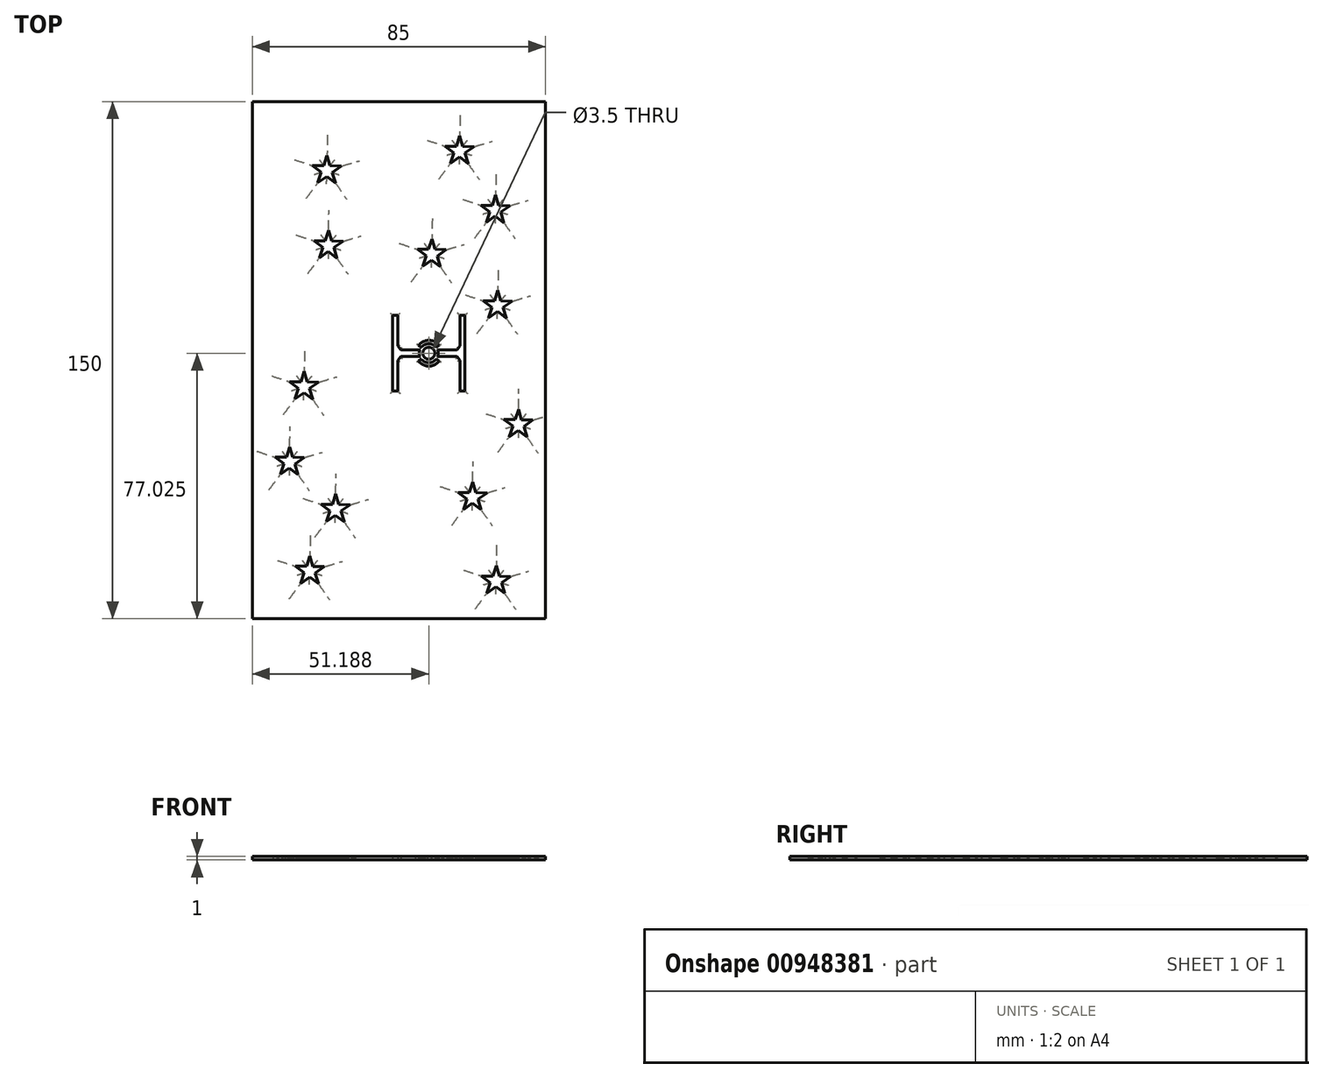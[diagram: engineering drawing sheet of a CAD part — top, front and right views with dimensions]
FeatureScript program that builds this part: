
annotation { "Feature Type Name" : "Feature", "Feature Type Description" : "" }
export const myFeature = defineFeature(function(context is Context, id is Id, definition is map)
    precondition{}
    {
        {
            var Q0;
            Q0=qCreatedBy(makeId("Top.planeOp"),FACE);
            var sketch = newSketch(context, id + "F0", { "sketchPlane" : qUnion([Q0])});
            skLineSegment(sketch, "E0.top", {"start": v(42.5, -75) * mm, "end": v(-42.5, -75) * mm});
            skLineSegment(sketch, "E0.left", {"start": v(42.5, 75) * mm, "end": v(42.5, -75) * mm});
            skLineSegment(sketch, "E0.right", {"start": v(-42.5, 75) * mm, "end": v(-42.5, -75) * mm});
            skLineSegment(sketch, "E1", {"start": v(-42.5, 75) * mm, "end": v(42.5, 75) * mm});
            skLineSegment(sketch, "E2", {"start": v(-1.81, 13.03) * mm, "end": v(-0.31, 13.03) * mm});
            skLineSegment(sketch, "E3", {"start": v(-0.31, 13.03) * mm, "end": v(-0.31, 4.14) * mm});
            skLineSegment(sketch, "E4", {"start": v(-0.31, 4.14) * mm, "end": v(0.54, 3) * mm});
            skLineSegment(sketch, "E5", {"start": v(0.54, 3) * mm, "end": v(6.12, 3) * mm});
            skLineSegment(sketch, "E6", {"start": v(-1.81, 13.03) * mm, "end": v(-1.81, -8.97) * mm});
            skPoint(sketch, "E7.endSnap0", {"position": v(-0.31, 8.58) * mm});
            skLineSegment(sketch, "E8.MirrorCS", {"start": v(0.54, 1.05) * mm, "end": v(6.12, 1.05) * mm});
            skLineSegment(sketch, "E9.MirrorCS", {"start": v(-0.31, -0.09) * mm, "end": v(0.54, 1.05) * mm});
            skLineSegment(sketch, "E10.MirrorCS", {"start": v(-0.31, -8.97) * mm, "end": v(-0.31, -0.09) * mm});
            skLineSegment(sketch, "E11.MirrorCS", {"start": v(-1.81, -8.97) * mm, "end": v(-0.31, -8.97) * mm});
            skLineSegment(sketch, "E12.MirrorCS", {"start": v(16.84, 3) * mm, "end": v(11.26, 3) * mm});
            skLineSegment(sketch, "E13.MirrorCS", {"start": v(16.84, 1.05) * mm, "end": v(11.26, 1.05) * mm});
            skLineSegment(sketch, "E14.MirrorCS", {"start": v(17.69, -0.09) * mm, "end": v(16.84, 1.05) * mm});
            skLineSegment(sketch, "E15.MirrorCS", {"start": v(17.69, 4.14) * mm, "end": v(16.84, 3) * mm});
            skLineSegment(sketch, "E16.MirrorCS", {"start": v(17.69, -8.97) * mm, "end": v(17.69, -0.09) * mm});
            skLineSegment(sketch, "E17.MirrorCS", {"start": v(19.19, -8.97) * mm, "end": v(17.69, -8.97) * mm});
            skLineSegment(sketch, "E18.MirrorCS", {"start": v(19.19, 13.03) * mm, "end": v(19.19, -8.97) * mm});
            skLineSegment(sketch, "E19.MirrorCS", {"start": v(19.19, 13.03) * mm, "end": v(17.69, 13.03) * mm});
            skLineSegment(sketch, "E20.MirrorCS", {"start": v(17.69, 13.03) * mm, "end": v(17.69, 4.14) * mm});
            skCircle(sketch, "E21", {"center": v(8.69, 2.03) * mm, "radius": 2.75 * mm});
            skCircle(sketch, "E22", {"center": v(8.69, 2.03) * mm, "radius": 1.75 * mm});
            skCircle(sketch, "E23", {"center": v(8.69, 2.03) * mm, "radius": 3.75 * mm});
            skLineSegment(sketch, "E24", {"start": v(6.52, 0.34) * mm, "end": v(5.69, -0.22) * mm});
            skLineSegment(sketch, "E25.MirrorCS", {"start": v(10.86, 0.34) * mm, "end": v(11.69, -0.22) * mm});
            skLineSegment(sketch, "E26.MirrorCS", {"start": v(6.52, 3.72) * mm, "end": v(5.69, 4.27) * mm});
            skLineSegment(sketch, "E27.MirrorCS", {"start": v(10.86, 3.72) * mm, "end": v(11.69, 4.27) * mm});
            skLineSegment(sketch, "E28", {"start": v(-20.37, 37.63) * mm, "end": v(-21.34, 34.62) * mm});
            skPoint(sketch, "E28.startSnap0", {"position": v(-20.37, 37.8) * mm});
            skLineSegment(sketch, "E29", {"start": v(-21.34, 34.62) * mm, "end": v(-24.61, 34.62) * mm});
            skLineSegment(sketch, "E30", {"start": v(-24.61, 34.62) * mm, "end": v(-22.04, 32.72) * mm});
            skLineSegment(sketch, "E31", {"start": v(-22.04, 32.72) * mm, "end": v(-23.07, 29.65) * mm});
            skLineSegment(sketch, "E32", {"start": v(-23.07, 29.65) * mm, "end": v(-20.47, 31.51) * mm});
            skLineSegment(sketch, "E33", {"start": v(-20.37, 37.63) * mm, "end": v(-20.47, 31.51) * mm, "construction": true});
            skLineSegment(sketch, "E34.MirrorCS", {"start": v(-17.93, 29.57) * mm, "end": v(-20.47, 31.51) * mm});
            skLineSegment(sketch, "E35.MirrorCS", {"start": v(-18.86, 32.67) * mm, "end": v(-17.93, 29.57) * mm});
            skLineSegment(sketch, "E36.MirrorCS", {"start": v(-16.23, 34.5) * mm, "end": v(-18.86, 32.67) * mm});
            skLineSegment(sketch, "E37.MirrorCS", {"start": v(-20.37, 37.63) * mm, "end": v(-19.5, 34.6) * mm});
            skLineSegment(sketch, "E38.MirrorCS", {"start": v(-19.5, 34.6) * mm, "end": v(-16.23, 34.5) * mm});
            skLineSegment(sketch, "E39", {"start": v(9.58, 35.19) * mm, "end": v(8.62, 32.18) * mm});
            skLineSegment(sketch, "E40", {"start": v(8.62, 32.18) * mm, "end": v(5.35, 32.18) * mm});
            skLineSegment(sketch, "E41", {"start": v(5.35, 32.18) * mm, "end": v(7.92, 30.28) * mm});
            skLineSegment(sketch, "E42", {"start": v(7.92, 30.28) * mm, "end": v(6.89, 27.2) * mm});
            skLineSegment(sketch, "E43", {"start": v(6.89, 27.2) * mm, "end": v(9.49, 29.07) * mm});
            skLineSegment(sketch, "E44.MirrorCS", {"start": v(12.03, 27.13) * mm, "end": v(9.49, 29.07) * mm});
            skLineSegment(sketch, "E45.MirrorCS", {"start": v(11.1, 30.23) * mm, "end": v(12.03, 27.13) * mm});
            skLineSegment(sketch, "E46.MirrorCS", {"start": v(13.73, 32.05) * mm, "end": v(11.1, 30.23) * mm});
            skLineSegment(sketch, "E47.MirrorCS", {"start": v(9.58, 35.19) * mm, "end": v(10.46, 32.15) * mm});
            skLineSegment(sketch, "E48.MirrorCS", {"start": v(10.46, 32.15) * mm, "end": v(13.73, 32.05) * mm});
            skLineSegment(sketch, "E49", {"start": v(-20.83, 59.45) * mm, "end": v(-21.8, 56.44) * mm});
            skLineSegment(sketch, "E50", {"start": v(-21.8, 56.44) * mm, "end": v(-25.06, 56.44) * mm});
            skLineSegment(sketch, "E51", {"start": v(-25.06, 56.44) * mm, "end": v(-22.5, 54.54) * mm});
            skLineSegment(sketch, "E52", {"start": v(-22.5, 54.54) * mm, "end": v(-23.52, 51.47) * mm});
            skLineSegment(sketch, "E53", {"start": v(-23.52, 51.47) * mm, "end": v(-20.92, 53.34) * mm});
            skLineSegment(sketch, "E54.MirrorCS", {"start": v(-18.38, 51.39) * mm, "end": v(-20.92, 53.34) * mm});
            skLineSegment(sketch, "E55.MirrorCS", {"start": v(-19.31, 54.5) * mm, "end": v(-18.38, 51.39) * mm});
            skLineSegment(sketch, "E56.MirrorCS", {"start": v(-16.68, 56.32) * mm, "end": v(-19.31, 54.5) * mm});
            skLineSegment(sketch, "E57.MirrorCS", {"start": v(-20.83, 59.45) * mm, "end": v(-19.95, 56.42) * mm});
            skLineSegment(sketch, "E58.MirrorCS", {"start": v(-19.95, 56.42) * mm, "end": v(-16.68, 56.32) * mm});
            skLineSegment(sketch, "E59", {"start": v(28.7, 20.23) * mm, "end": v(27.73, 17.23) * mm});
            skLineSegment(sketch, "E60", {"start": v(27.73, 17.23) * mm, "end": v(24.46, 17.23) * mm});
            skLineSegment(sketch, "E61", {"start": v(24.46, 17.23) * mm, "end": v(27.03, 15.32) * mm});
            skLineSegment(sketch, "E62", {"start": v(27.03, 15.32) * mm, "end": v(26, 12.25) * mm});
            skLineSegment(sketch, "E63", {"start": v(26, 12.25) * mm, "end": v(28.6, 14.12) * mm});
            skLineSegment(sketch, "E64.MirrorCS", {"start": v(31.14, 12.17) * mm, "end": v(28.6, 14.12) * mm});
            skLineSegment(sketch, "E65.MirrorCS", {"start": v(30.2, 15.27) * mm, "end": v(31.14, 12.17) * mm});
            skLineSegment(sketch, "E66.MirrorCS", {"start": v(32.84, 17.1) * mm, "end": v(30.2, 15.27) * mm});
            skLineSegment(sketch, "E67.MirrorCS", {"start": v(28.7, 20.23) * mm, "end": v(29.57, 17.2) * mm});
            skLineSegment(sketch, "E68.MirrorCS", {"start": v(29.57, 17.2) * mm, "end": v(32.84, 17.1) * mm});
            skLineSegment(sketch, "E69", {"start": v(21.4, -35.35) * mm, "end": v(20.44, -38.35) * mm});
            skLineSegment(sketch, "E70", {"start": v(20.44, -38.35) * mm, "end": v(17.17, -38.35) * mm});
            skLineSegment(sketch, "E71", {"start": v(17.17, -38.35) * mm, "end": v(19.74, -40.26) * mm});
            skLineSegment(sketch, "E72", {"start": v(19.74, -40.26) * mm, "end": v(18.71, -43.33) * mm});
            skLineSegment(sketch, "E73", {"start": v(18.71, -43.33) * mm, "end": v(21.31, -41.46) * mm});
            skLineSegment(sketch, "E74.MirrorCS", {"start": v(23.86, -43.41) * mm, "end": v(21.31, -41.46) * mm});
            skLineSegment(sketch, "E75.MirrorCS", {"start": v(22.92, -40.3) * mm, "end": v(23.86, -43.41) * mm});
            skLineSegment(sketch, "E76.MirrorCS", {"start": v(25.55, -38.48) * mm, "end": v(22.92, -40.3) * mm});
            skLineSegment(sketch, "E77.MirrorCS", {"start": v(21.4, -35.35) * mm, "end": v(22.28, -38.38) * mm});
            skLineSegment(sketch, "E78.MirrorCS", {"start": v(22.28, -38.38) * mm, "end": v(25.55, -38.48) * mm});
            skLineSegment(sketch, "E79", {"start": v(-18.3, -38.84) * mm, "end": v(-19.28, -41.84) * mm});
            skLineSegment(sketch, "E80", {"start": v(-19.28, -41.84) * mm, "end": v(-22.55, -41.84) * mm});
            skLineSegment(sketch, "E81", {"start": v(-22.55, -41.84) * mm, "end": v(-19.97, -43.75) * mm});
            skLineSegment(sketch, "E82", {"start": v(-19.97, -43.75) * mm, "end": v(-21, -46.82) * mm});
            skLineSegment(sketch, "E83", {"start": v(-21, -46.82) * mm, "end": v(-18.4, -44.95) * mm});
            skLineSegment(sketch, "E84.MirrorCS", {"start": v(-15.86, -46.9) * mm, "end": v(-18.4, -44.95) * mm});
            skLineSegment(sketch, "E85.MirrorCS", {"start": v(-16.8, -43.8) * mm, "end": v(-15.86, -46.9) * mm});
            skLineSegment(sketch, "E86.MirrorCS", {"start": v(-14.17, -41.97) * mm, "end": v(-16.8, -43.8) * mm});
            skLineSegment(sketch, "E87.MirrorCS", {"start": v(-18.3, -38.84) * mm, "end": v(-17.43, -41.87) * mm});
            skLineSegment(sketch, "E88.MirrorCS", {"start": v(-17.43, -41.87) * mm, "end": v(-14.17, -41.97) * mm});
            skLineSegment(sketch, "E89", {"start": v(-27.45, -3.28) * mm, "end": v(-28.42, -6.28) * mm});
            skLineSegment(sketch, "E90", {"start": v(-28.42, -6.28) * mm, "end": v(-31.69, -6.28) * mm});
            skLineSegment(sketch, "E91", {"start": v(-31.69, -6.28) * mm, "end": v(-29.11, -8.19) * mm});
            skLineSegment(sketch, "E92", {"start": v(-29.11, -8.19) * mm, "end": v(-30.14, -11.26) * mm});
            skLineSegment(sketch, "E93", {"start": v(-30.14, -11.26) * mm, "end": v(-27.54, -9.4) * mm});
            skLineSegment(sketch, "E94.MirrorCS", {"start": v(-25, -11.34) * mm, "end": v(-27.54, -9.4) * mm});
            skLineSegment(sketch, "E95.MirrorCS", {"start": v(-25.93, -8.24) * mm, "end": v(-25, -11.34) * mm});
            skLineSegment(sketch, "E96.MirrorCS", {"start": v(-23.3, -6.41) * mm, "end": v(-25.93, -8.24) * mm});
            skLineSegment(sketch, "E97.MirrorCS", {"start": v(-27.45, -3.28) * mm, "end": v(-26.57, -6.31) * mm});
            skLineSegment(sketch, "E98.MirrorCS", {"start": v(-26.57, -6.31) * mm, "end": v(-23.3, -6.41) * mm});
            skLineSegment(sketch, "E99", {"start": v(28.22, -59.61) * mm, "end": v(27.25, -62.62) * mm});
            skLineSegment(sketch, "E100", {"start": v(27.25, -62.62) * mm, "end": v(23.98, -62.62) * mm});
            skLineSegment(sketch, "E101", {"start": v(23.98, -62.62) * mm, "end": v(26.55, -64.52) * mm});
            skLineSegment(sketch, "E102", {"start": v(26.55, -64.52) * mm, "end": v(25.52, -67.6) * mm});
            skLineSegment(sketch, "E103", {"start": v(25.52, -67.6) * mm, "end": v(28.13, -65.72) * mm});
            skLineSegment(sketch, "E104.MirrorCS", {"start": v(30.67, -67.67) * mm, "end": v(28.13, -65.72) * mm});
            skLineSegment(sketch, "E105.MirrorCS", {"start": v(29.73, -64.57) * mm, "end": v(30.67, -67.67) * mm});
            skLineSegment(sketch, "E106.MirrorCS", {"start": v(32.36, -62.75) * mm, "end": v(29.73, -64.57) * mm});
            skLineSegment(sketch, "E107.MirrorCS", {"start": v(28.22, -59.61) * mm, "end": v(29.1, -62.64) * mm});
            skLineSegment(sketch, "E108.MirrorCS", {"start": v(29.1, -62.64) * mm, "end": v(32.36, -62.75) * mm});
            skLineSegment(sketch, "E109", {"start": v(34.7, -14.25) * mm, "end": v(33.73, -17.25) * mm});
            skLineSegment(sketch, "E110", {"start": v(33.73, -17.25) * mm, "end": v(30.46, -17.25) * mm});
            skLineSegment(sketch, "E111", {"start": v(30.46, -17.25) * mm, "end": v(33.04, -19.15) * mm});
            skLineSegment(sketch, "E112", {"start": v(33.04, -19.15) * mm, "end": v(32, -22.23) * mm});
            skLineSegment(sketch, "E113", {"start": v(32, -22.23) * mm, "end": v(34.6, -20.36) * mm});
            skLineSegment(sketch, "E114.MirrorCS", {"start": v(37.15, -22.3) * mm, "end": v(34.6, -20.36) * mm});
            skLineSegment(sketch, "E115.MirrorCS", {"start": v(36.22, -19.2) * mm, "end": v(37.15, -22.3) * mm});
            skLineSegment(sketch, "E116.MirrorCS", {"start": v(38.84, -17.38) * mm, "end": v(36.22, -19.2) * mm});
            skLineSegment(sketch, "E117.MirrorCS", {"start": v(34.7, -14.25) * mm, "end": v(35.58, -17.28) * mm});
            skLineSegment(sketch, "E118.MirrorCS", {"start": v(35.58, -17.28) * mm, "end": v(38.84, -17.38) * mm});
            skLineSegment(sketch, "E119", {"start": v(-25.79, -56.79) * mm, "end": v(-26.75, -59.8) * mm});
            skLineSegment(sketch, "E120", {"start": v(-26.75, -59.8) * mm, "end": v(-30.02, -59.8) * mm});
            skLineSegment(sketch, "E121", {"start": v(-30.02, -59.8) * mm, "end": v(-27.45, -61.7) * mm});
            skLineSegment(sketch, "E122", {"start": v(-27.45, -61.7) * mm, "end": v(-28.48, -64.77) * mm});
            skLineSegment(sketch, "E123", {"start": v(-28.48, -64.77) * mm, "end": v(-25.88, -62.9) * mm});
            skLineSegment(sketch, "E124.MirrorCS", {"start": v(-23.34, -64.85) * mm, "end": v(-25.88, -62.9) * mm});
            skLineSegment(sketch, "E125.MirrorCS", {"start": v(-24.27, -61.74) * mm, "end": v(-23.34, -64.85) * mm});
            skLineSegment(sketch, "E126.MirrorCS", {"start": v(-21.64, -59.92) * mm, "end": v(-24.27, -61.74) * mm});
            skLineSegment(sketch, "E127.MirrorCS", {"start": v(-25.79, -56.79) * mm, "end": v(-24.91, -59.82) * mm});
            skLineSegment(sketch, "E128.MirrorCS", {"start": v(-24.91, -59.82) * mm, "end": v(-21.64, -59.92) * mm});
            skLineSegment(sketch, "E129", {"start": v(17.65, 65.09) * mm, "end": v(16.68, 62.09) * mm});
            skLineSegment(sketch, "E130", {"start": v(16.68, 62.09) * mm, "end": v(13.41, 62.09) * mm});
            skLineSegment(sketch, "E131", {"start": v(13.41, 62.09) * mm, "end": v(15.98, 60.18) * mm});
            skLineSegment(sketch, "E132", {"start": v(15.98, 60.18) * mm, "end": v(14.95, 57.1) * mm});
            skLineSegment(sketch, "E133", {"start": v(14.95, 57.1) * mm, "end": v(17.55, 58.98) * mm});
            skLineSegment(sketch, "E134.MirrorCS", {"start": v(20.1, 57.03) * mm, "end": v(17.55, 58.98) * mm});
            skLineSegment(sketch, "E135.MirrorCS", {"start": v(19.16, 60.13) * mm, "end": v(20.1, 57.03) * mm});
            skLineSegment(sketch, "E136.MirrorCS", {"start": v(21.8, 61.96) * mm, "end": v(19.16, 60.13) * mm});
            skLineSegment(sketch, "E137.MirrorCS", {"start": v(17.65, 65.09) * mm, "end": v(18.52, 62.06) * mm});
            skLineSegment(sketch, "E138.MirrorCS", {"start": v(18.52, 62.06) * mm, "end": v(21.8, 61.96) * mm});
            skLineSegment(sketch, "E139", {"start": v(28.04, 47.95) * mm, "end": v(27.07, 44.94) * mm});
            skLineSegment(sketch, "E140", {"start": v(27.07, 44.94) * mm, "end": v(23.8, 44.94) * mm});
            skLineSegment(sketch, "E141", {"start": v(23.8, 44.94) * mm, "end": v(26.37, 43.04) * mm});
            skLineSegment(sketch, "E142", {"start": v(26.37, 43.04) * mm, "end": v(25.34, 39.97) * mm});
            skLineSegment(sketch, "E143", {"start": v(25.34, 39.97) * mm, "end": v(27.95, 41.84) * mm});
            skLineSegment(sketch, "E144.MirrorCS", {"start": v(30.49, 39.89) * mm, "end": v(27.95, 41.84) * mm});
            skLineSegment(sketch, "E145.MirrorCS", {"start": v(29.55, 43) * mm, "end": v(30.49, 39.89) * mm});
            skLineSegment(sketch, "E146.MirrorCS", {"start": v(32.18, 44.82) * mm, "end": v(29.55, 43) * mm});
            skLineSegment(sketch, "E147.MirrorCS", {"start": v(28.04, 47.95) * mm, "end": v(28.91, 44.92) * mm});
            skLineSegment(sketch, "E148.MirrorCS", {"start": v(28.91, 44.92) * mm, "end": v(32.18, 44.82) * mm});
            skLineSegment(sketch, "E149", {"start": v(-31.65, -25.14) * mm, "end": v(-32.62, -28.14) * mm});
            skLineSegment(sketch, "E150", {"start": v(-32.62, -28.14) * mm, "end": v(-35.89, -28.14) * mm});
            skLineSegment(sketch, "E151", {"start": v(-35.89, -28.14) * mm, "end": v(-33.32, -30.05) * mm});
            skLineSegment(sketch, "E152", {"start": v(-33.32, -30.05) * mm, "end": v(-34.35, -33.12) * mm});
            skLineSegment(sketch, "E153", {"start": v(-34.35, -33.12) * mm, "end": v(-31.75, -31.25) * mm});
            skLineSegment(sketch, "E154.MirrorCS", {"start": v(-29.2, -33.2) * mm, "end": v(-31.75, -31.25) * mm});
            skLineSegment(sketch, "E155.MirrorCS", {"start": v(-30.14, -30.1) * mm, "end": v(-29.2, -33.2) * mm});
            skLineSegment(sketch, "E156.MirrorCS", {"start": v(-27.5, -28.27) * mm, "end": v(-30.14, -30.1) * mm});
            skLineSegment(sketch, "E157.MirrorCS", {"start": v(-31.65, -25.14) * mm, "end": v(-30.78, -28.17) * mm});
            skLineSegment(sketch, "E158.MirrorCS", {"start": v(-30.78, -28.17) * mm, "end": v(-27.5, -28.27) * mm});
            skSolve(sketch);
        }
        {
            var Q0;
            Q0=makeQuery(id+"F0.imprint","IMPRINT",FACE,{"disambiguationData":[TD([[makeQuery(id+"F0.imprint","IMPRINT",EDGE,{"derivedFrom":sQuery(id+"F0.wireOp",EDGE,"E0.top")}),-1.0]])]});
            var Q1;
            Q1=makeQuery(id+"F0.imprint","IMPRINT",FACE,{"disambiguationData":[TD([[makeQuery(id+"F0.imprint","IMPRINT",EDGE,{"derivedFrom":sQuery(id+"F0.wireOp",EDGE,"E22")}),-1.0]])]});
            var Q2;
            {var subQ5=sQuery(id+"F0.wireOp",EDGE,"E24");Q2=makeQuery(id+"F0.imprint","IMPRINT",FACE,{"disambiguationData":[TD([[makeQuery(id+"F0.imprint","IMPRINT",EDGE,{"derivedFrom":subQ5}),-1.0]])]});}
            var Q3;
            {var subQ5=sQuery(id+"F0.wireOp",EDGE,"E26.MirrorCS");Q3=makeQuery(id+"F0.imprint","IMPRINT",FACE,{"disambiguationData":[TD([[makeQuery(id+"F0.imprint","IMPRINT",EDGE,{"derivedFrom":subQ5}),1.0]])]});}
            var Q4;
            {var subQ5=sQuery(id+"F0.wireOp",EDGE,"E25.MirrorCS");Q4=makeQuery(id+"F0.imprint","IMPRINT",FACE,{"disambiguationData":[TD([[makeQuery(id+"F0.imprint","IMPRINT",EDGE,{"derivedFrom":subQ5}),1.0]])]});}
            var Q5;
            {var subQ5=sQuery(id+"F0.wireOp",EDGE,"E27.MirrorCS");Q5=makeQuery(id+"F0.imprint","IMPRINT",FACE,{"disambiguationData":[TD([[makeQuery(id+"F0.imprint","IMPRINT",EDGE,{"derivedFrom":subQ5}),-1.0]])]});}
            extrude(context, id + "F1", {"entities" : qUnion([Q0, Q1, Q2, Q3, Q4, Q5]), "depth" : 1 * mm, "offsetDistance" : 25 * mm});
        }
        {
            var Q0;
            Q0=makeQuery(id+"F1.opExtrude","CAP_EDGE",EDGE,{"disambiguationData":[OSD([sQuery(id+"F0.wireOp",EDGE,"E147.MirrorCS")])],"isStart":true});
            var Q1;
            Q1=makeQuery(id+"F1.opExtrude","CAP_EDGE",EDGE,{"disambiguationData":[OSD([sQuery(id+"F0.wireOp",EDGE,"E148.MirrorCS")])],"isStart":true});
            var Q2;
            Q2=makeQuery(id+"F1.opExtrude","CAP_EDGE",EDGE,{"disambiguationData":[OSD([sQuery(id+"F0.wireOp",EDGE,"E146.MirrorCS")])],"isStart":true});
            var Q3;
            Q3=makeQuery(id+"F1.opExtrude","CAP_EDGE",EDGE,{"disambiguationData":[OSD([sQuery(id+"F0.wireOp",EDGE,"E145.MirrorCS")])],"isStart":true});
            var Q4;
            Q4=makeQuery(id+"F1.opExtrude","CAP_EDGE",EDGE,{"disambiguationData":[OSD([sQuery(id+"F0.wireOp",EDGE,"E144.MirrorCS")])],"isStart":true});
            var Q5;
            Q5=makeQuery(id+"F1.opExtrude","CAP_EDGE",EDGE,{"disambiguationData":[OSD([sQuery(id+"F0.wireOp",EDGE,"E143")])],"isStart":true});
            var Q6;
            Q6=makeQuery(id+"F1.opExtrude","CAP_EDGE",EDGE,{"disambiguationData":[OSD([sQuery(id+"F0.wireOp",EDGE,"E142")])],"isStart":true});
            var Q7;
            Q7=makeQuery(id+"F1.opExtrude","CAP_EDGE",EDGE,{"disambiguationData":[OSD([sQuery(id+"F0.wireOp",EDGE,"E141")])],"isStart":true});
            var Q8;
            Q8=makeQuery(id+"F1.opExtrude","CAP_EDGE",EDGE,{"disambiguationData":[OSD([sQuery(id+"F0.wireOp",EDGE,"E140")])],"isStart":true});
            var Q9;
            Q9=makeQuery(id+"F1.opExtrude","CAP_EDGE",EDGE,{"disambiguationData":[OSD([sQuery(id+"F0.wireOp",EDGE,"E139")])],"isStart":true});
            var Q10;
            Q10=makeQuery(id+"F1.opExtrude","CAP_EDGE",EDGE,{"disambiguationData":[OSD([sQuery(id+"F0.wireOp",EDGE,"E48.MirrorCS")])],"isStart":true});
            var Q11;
            Q11=makeQuery(id+"F1.opExtrude","CAP_EDGE",EDGE,{"disambiguationData":[OSD([sQuery(id+"F0.wireOp",EDGE,"E47.MirrorCS")])],"isStart":true});
            var Q12;
            Q12=makeQuery(id+"F1.opExtrude","CAP_EDGE",EDGE,{"disambiguationData":[OSD([sQuery(id+"F0.wireOp",EDGE,"E39")])],"isStart":true});
            var Q13;
            Q13=makeQuery(id+"F1.opExtrude","CAP_EDGE",EDGE,{"disambiguationData":[OSD([sQuery(id+"F0.wireOp",EDGE,"E40")])],"isStart":true});
            var Q14;
            Q14=makeQuery(id+"F1.opExtrude","CAP_EDGE",EDGE,{"disambiguationData":[OSD([sQuery(id+"F0.wireOp",EDGE,"E41")])],"isStart":true});
            var Q15;
            Q15=makeQuery(id+"F1.opExtrude","CAP_EDGE",EDGE,{"disambiguationData":[OSD([sQuery(id+"F0.wireOp",EDGE,"E42")])],"isStart":true});
            var Q16;
            Q16=makeQuery(id+"F1.opExtrude","CAP_EDGE",EDGE,{"disambiguationData":[OSD([sQuery(id+"F0.wireOp",EDGE,"E43")])],"isStart":true});
            var Q17;
            Q17=makeQuery(id+"F1.opExtrude","CAP_EDGE",EDGE,{"disambiguationData":[OSD([sQuery(id+"F0.wireOp",EDGE,"E44.MirrorCS")])],"isStart":true});
            var Q18;
            Q18=makeQuery(id+"F1.opExtrude","CAP_EDGE",EDGE,{"disambiguationData":[OSD([sQuery(id+"F0.wireOp",EDGE,"E45.MirrorCS")])],"isStart":true});
            var Q19;
            Q19=makeQuery(id+"F1.opExtrude","CAP_EDGE",EDGE,{"disambiguationData":[OSD([sQuery(id+"F0.wireOp",EDGE,"E46.MirrorCS")])],"isStart":true});
            var Q20;
            Q20=makeQuery(id+"F1.opExtrude","CAP_EDGE",EDGE,{"disambiguationData":[OSD([sQuery(id+"F0.wireOp",EDGE,"E36.MirrorCS")])],"isStart":true});
            var Q21;
            Q21=makeQuery(id+"F1.opExtrude","CAP_EDGE",EDGE,{"disambiguationData":[OSD([sQuery(id+"F0.wireOp",EDGE,"E35.MirrorCS")])],"isStart":true});
            var Q22;
            Q22=makeQuery(id+"F1.opExtrude","CAP_EDGE",EDGE,{"disambiguationData":[OSD([sQuery(id+"F0.wireOp",EDGE,"E34.MirrorCS")])],"isStart":true});
            var Q23;
            Q23=makeQuery(id+"F1.opExtrude","CAP_EDGE",EDGE,{"disambiguationData":[OSD([sQuery(id+"F0.wireOp",EDGE,"E32")])],"isStart":true});
            var Q24;
            Q24=makeQuery(id+"F1.opExtrude","CAP_EDGE",EDGE,{"disambiguationData":[OSD([sQuery(id+"F0.wireOp",EDGE,"E31")])],"isStart":true});
            var Q25;
            Q25=makeQuery(id+"F1.opExtrude","CAP_EDGE",EDGE,{"disambiguationData":[OSD([sQuery(id+"F0.wireOp",EDGE,"E30")])],"isStart":true});
            var Q26;
            Q26=makeQuery(id+"F1.opExtrude","CAP_EDGE",EDGE,{"disambiguationData":[OSD([sQuery(id+"F0.wireOp",EDGE,"E29")])],"isStart":true});
            var Q27;
            Q27=makeQuery(id+"F1.opExtrude","CAP_EDGE",EDGE,{"disambiguationData":[OSD([sQuery(id+"F0.wireOp",EDGE,"E28")])],"isStart":true});
            var Q28;
            Q28=makeQuery(id+"F1.opExtrude","CAP_EDGE",EDGE,{"disambiguationData":[OSD([sQuery(id+"F0.wireOp",EDGE,"E37.MirrorCS")])],"isStart":true});
            var Q29;
            Q29=makeQuery(id+"F1.opExtrude","CAP_EDGE",EDGE,{"disambiguationData":[OSD([sQuery(id+"F0.wireOp",EDGE,"E38.MirrorCS")])],"isStart":true});
            var Q30;
            Q30=makeQuery(id+"F1.opExtrude","CAP_EDGE",EDGE,{"disambiguationData":[OSD([sQuery(id+"F0.wireOp",EDGE,"E137.MirrorCS")])],"isStart":true});
            var Q31;
            Q31=makeQuery(id+"F1.opExtrude","CAP_EDGE",EDGE,{"disambiguationData":[OSD([sQuery(id+"F0.wireOp",EDGE,"E138.MirrorCS")])],"isStart":true});
            var Q32;
            Q32=makeQuery(id+"F1.opExtrude","CAP_EDGE",EDGE,{"disambiguationData":[OSD([sQuery(id+"F0.wireOp",EDGE,"E136.MirrorCS")])],"isStart":true});
            var Q33;
            Q33=makeQuery(id+"F1.opExtrude","CAP_EDGE",EDGE,{"disambiguationData":[OSD([sQuery(id+"F0.wireOp",EDGE,"E135.MirrorCS")])],"isStart":true});
            var Q34;
            Q34=makeQuery(id+"F1.opExtrude","CAP_EDGE",EDGE,{"disambiguationData":[OSD([sQuery(id+"F0.wireOp",EDGE,"E134.MirrorCS")])],"isStart":true});
            var Q35;
            Q35=makeQuery(id+"F1.opExtrude","CAP_EDGE",EDGE,{"disambiguationData":[OSD([sQuery(id+"F0.wireOp",EDGE,"E133")])],"isStart":true});
            var Q36;
            Q36=makeQuery(id+"F1.opExtrude","CAP_EDGE",EDGE,{"disambiguationData":[OSD([sQuery(id+"F0.wireOp",EDGE,"E132")])],"isStart":true});
            var Q37;
            Q37=makeQuery(id+"F1.opExtrude","CAP_EDGE",EDGE,{"disambiguationData":[OSD([sQuery(id+"F0.wireOp",EDGE,"E131")])],"isStart":true});
            var Q38;
            Q38=makeQuery(id+"F1.opExtrude","CAP_EDGE",EDGE,{"disambiguationData":[OSD([sQuery(id+"F0.wireOp",EDGE,"E130")])],"isStart":true});
            var Q39;
            Q39=makeQuery(id+"F1.opExtrude","CAP_EDGE",EDGE,{"disambiguationData":[OSD([sQuery(id+"F0.wireOp",EDGE,"E129")])],"isStart":true});
            var Q40;
            Q40=makeQuery(id+"F1.opExtrude","CAP_EDGE",EDGE,{"disambiguationData":[OSD([sQuery(id+"F0.wireOp",EDGE,"E51")])],"isStart":true});
            var Q41;
            Q41=makeQuery(id+"F1.opExtrude","CAP_EDGE",EDGE,{"disambiguationData":[OSD([sQuery(id+"F0.wireOp",EDGE,"E52")])],"isStart":true});
            var Q42;
            Q42=makeQuery(id+"F1.opExtrude","CAP_EDGE",EDGE,{"disambiguationData":[OSD([sQuery(id+"F0.wireOp",EDGE,"E53")])],"isStart":true});
            var Q43;
            Q43=makeQuery(id+"F1.opExtrude","CAP_EDGE",EDGE,{"disambiguationData":[OSD([sQuery(id+"F0.wireOp",EDGE,"E54.MirrorCS")])],"isStart":true});
            var Q44;
            Q44=makeQuery(id+"F1.opExtrude","CAP_EDGE",EDGE,{"disambiguationData":[OSD([sQuery(id+"F0.wireOp",EDGE,"E55.MirrorCS")])],"isStart":true});
            var Q45;
            Q45=makeQuery(id+"F1.opExtrude","CAP_EDGE",EDGE,{"disambiguationData":[OSD([sQuery(id+"F0.wireOp",EDGE,"E56.MirrorCS")])],"isStart":true});
            var Q46;
            Q46=makeQuery(id+"F1.opExtrude","CAP_EDGE",EDGE,{"disambiguationData":[OSD([sQuery(id+"F0.wireOp",EDGE,"E58.MirrorCS")])],"isStart":true});
            var Q47;
            Q47=makeQuery(id+"F1.opExtrude","CAP_EDGE",EDGE,{"disambiguationData":[OSD([sQuery(id+"F0.wireOp",EDGE,"E57.MirrorCS")])],"isStart":true});
            var Q48;
            Q48=makeQuery(id+"F1.opExtrude","CAP_EDGE",EDGE,{"disambiguationData":[OSD([sQuery(id+"F0.wireOp",EDGE,"E49")])],"isStart":true});
            var Q49;
            Q49=makeQuery(id+"F1.opExtrude","CAP_EDGE",EDGE,{"disambiguationData":[OSD([sQuery(id+"F0.wireOp",EDGE,"E50")])],"isStart":true});
            var Q50;
            Q50=makeQuery(id+"F1.opExtrude","CAP_EDGE",EDGE,{"disambiguationData":[OSD([sQuery(id+"F0.wireOp",EDGE,"E68.MirrorCS")])],"isStart":true});
            var Q51;
            Q51=makeQuery(id+"F1.opExtrude","CAP_EDGE",EDGE,{"disambiguationData":[OSD([sQuery(id+"F0.wireOp",EDGE,"E67.MirrorCS")])],"isStart":true});
            var Q52;
            Q52=makeQuery(id+"F1.opExtrude","CAP_EDGE",EDGE,{"disambiguationData":[OSD([sQuery(id+"F0.wireOp",EDGE,"E59")])],"isStart":true});
            var Q53;
            Q53=makeQuery(id+"F1.opExtrude","CAP_EDGE",EDGE,{"disambiguationData":[OSD([sQuery(id+"F0.wireOp",EDGE,"E60")])],"isStart":true});
            var Q54;
            Q54=makeQuery(id+"F1.opExtrude","CAP_EDGE",EDGE,{"disambiguationData":[OSD([sQuery(id+"F0.wireOp",EDGE,"E61")])],"isStart":true});
            var Q55;
            Q55=makeQuery(id+"F1.opExtrude","CAP_EDGE",EDGE,{"disambiguationData":[OSD([sQuery(id+"F0.wireOp",EDGE,"E62")])],"isStart":true});
            var Q56;
            Q56=makeQuery(id+"F1.opExtrude","CAP_EDGE",EDGE,{"disambiguationData":[OSD([sQuery(id+"F0.wireOp",EDGE,"E63")])],"isStart":true});
            var Q57;
            Q57=makeQuery(id+"F1.opExtrude","CAP_EDGE",EDGE,{"disambiguationData":[OSD([sQuery(id+"F0.wireOp",EDGE,"E64.MirrorCS")])],"isStart":true});
            var Q58;
            Q58=makeQuery(id+"F1.opExtrude","CAP_EDGE",EDGE,{"disambiguationData":[OSD([sQuery(id+"F0.wireOp",EDGE,"E65.MirrorCS")])],"isStart":true});
            var Q59;
            Q59=makeQuery(id+"F1.opExtrude","CAP_EDGE",EDGE,{"disambiguationData":[OSD([sQuery(id+"F0.wireOp",EDGE,"E66.MirrorCS")])],"isStart":true});
            var Q60;
            Q60=makeQuery(id+"F1.opExtrude","CAP_EDGE",EDGE,{"disambiguationData":[OSD([sQuery(id+"F0.wireOp",EDGE,"E98.MirrorCS")])],"isStart":true});
            var Q61;
            Q61=makeQuery(id+"F1.opExtrude","CAP_EDGE",EDGE,{"disambiguationData":[OSD([sQuery(id+"F0.wireOp",EDGE,"E97.MirrorCS")])],"isStart":true});
            var Q62;
            Q62=makeQuery(id+"F1.opExtrude","CAP_EDGE",EDGE,{"disambiguationData":[OSD([sQuery(id+"F0.wireOp",EDGE,"E89")])],"isStart":true});
            var Q63;
            Q63=makeQuery(id+"F1.opExtrude","CAP_EDGE",EDGE,{"disambiguationData":[OSD([sQuery(id+"F0.wireOp",EDGE,"E90")])],"isStart":true});
            var Q64;
            Q64=makeQuery(id+"F1.opExtrude","CAP_EDGE",EDGE,{"disambiguationData":[OSD([sQuery(id+"F0.wireOp",EDGE,"E91")])],"isStart":true});
            var Q65;
            Q65=makeQuery(id+"F1.opExtrude","CAP_EDGE",EDGE,{"disambiguationData":[OSD([sQuery(id+"F0.wireOp",EDGE,"E93")])],"isStart":true});
            var Q66;
            Q66=makeQuery(id+"F1.opExtrude","CAP_EDGE",EDGE,{"disambiguationData":[OSD([sQuery(id+"F0.wireOp",EDGE,"E94.MirrorCS")])],"isStart":true});
            var Q67;
            Q67=makeQuery(id+"F1.opExtrude","CAP_EDGE",EDGE,{"disambiguationData":[OSD([sQuery(id+"F0.wireOp",EDGE,"E95.MirrorCS")])],"isStart":true});
            var Q68;
            Q68=makeQuery(id+"F1.opExtrude","CAP_EDGE",EDGE,{"disambiguationData":[OSD([sQuery(id+"F0.wireOp",EDGE,"E96.MirrorCS")])],"isStart":true});
            var Q69;
            Q69=makeQuery(id+"F1.opExtrude","CAP_EDGE",EDGE,{"disambiguationData":[OSD([sQuery(id+"F0.wireOp",EDGE,"E92")])],"isStart":true});
            fillet(context, id + "F2", {"entities" : qUnion([Q0, Q1, Q2, Q3, Q4, Q5, Q6, Q7, Q8, Q9, Q10, Q11, Q12, Q13, Q14, Q15, Q16, Q17, Q18, Q19, Q20, Q21, Q22, Q23, Q24, Q25, Q26, Q27, Q28, Q29, Q30, Q31, Q32, Q33, Q34, Q35, Q36, Q37, Q38, Q39, Q40, Q41, Q42, Q43, Q44, Q45, Q46, Q47, Q48, Q49, Q50, Q51, Q52, Q53, Q54, Q55, Q56, Q57, Q58, Q59, Q60, Q61, Q62, Q63, Q64, Q65, Q66, Q67, Q68, Q69]), "radius" : 2 * mm, "tangentPropagation" : true, "allowEdgeOverflow" : false});
        }
        {
            var Q0;
            Q0=makeQuery(id+"F1.opExtrude","CAP_EDGE",EDGE,{"disambiguationData":[OSD([sQuery(id+"F0.wireOp",EDGE,"E150")])],"isStart":true});
            var Q1;
            Q1=makeQuery(id+"F1.opExtrude","CAP_EDGE",EDGE,{"disambiguationData":[OSD([sQuery(id+"F0.wireOp",EDGE,"E149")])],"isStart":true});
            var Q2;
            Q2=makeQuery(id+"F1.opExtrude","CAP_EDGE",EDGE,{"disambiguationData":[OSD([sQuery(id+"F0.wireOp",EDGE,"E157.MirrorCS")])],"isStart":true});
            var Q3;
            Q3=makeQuery(id+"F1.opExtrude","CAP_EDGE",EDGE,{"disambiguationData":[OSD([sQuery(id+"F0.wireOp",EDGE,"E158.MirrorCS")])],"isStart":true});
            var Q4;
            Q4=makeQuery(id+"F1.opExtrude","CAP_EDGE",EDGE,{"disambiguationData":[OSD([sQuery(id+"F0.wireOp",EDGE,"E156.MirrorCS")])],"isStart":true});
            var Q5;
            Q5=makeQuery(id+"F1.opExtrude","CAP_EDGE",EDGE,{"disambiguationData":[OSD([sQuery(id+"F0.wireOp",EDGE,"E155.MirrorCS")])],"isStart":true});
            var Q6;
            Q6=makeQuery(id+"F1.opExtrude","CAP_EDGE",EDGE,{"disambiguationData":[OSD([sQuery(id+"F0.wireOp",EDGE,"E154.MirrorCS")])],"isStart":true});
            var Q7;
            Q7=makeQuery(id+"F1.opExtrude","CAP_EDGE",EDGE,{"disambiguationData":[OSD([sQuery(id+"F0.wireOp",EDGE,"E153")])],"isStart":true});
            var Q8;
            Q8=makeQuery(id+"F1.opExtrude","CAP_EDGE",EDGE,{"disambiguationData":[OSD([sQuery(id+"F0.wireOp",EDGE,"E152")])],"isStart":true});
            var Q9;
            Q9=makeQuery(id+"F1.opExtrude","CAP_EDGE",EDGE,{"disambiguationData":[OSD([sQuery(id+"F0.wireOp",EDGE,"E151")])],"isStart":true});
            var Q10;
            Q10=makeQuery(id+"F1.opExtrude","CAP_EDGE",EDGE,{"disambiguationData":[OSD([sQuery(id+"F0.wireOp",EDGE,"E83")])],"isStart":true});
            var Q11;
            Q11=makeQuery(id+"F1.opExtrude","CAP_EDGE",EDGE,{"disambiguationData":[OSD([sQuery(id+"F0.wireOp",EDGE,"E82")])],"isStart":true});
            var Q12;
            Q12=makeQuery(id+"F1.opExtrude","CAP_EDGE",EDGE,{"disambiguationData":[OSD([sQuery(id+"F0.wireOp",EDGE,"E81")])],"isStart":true});
            var Q13;
            Q13=makeQuery(id+"F1.opExtrude","CAP_EDGE",EDGE,{"disambiguationData":[OSD([sQuery(id+"F0.wireOp",EDGE,"E80")])],"isStart":true});
            var Q14;
            Q14=makeQuery(id+"F1.opExtrude","CAP_EDGE",EDGE,{"disambiguationData":[OSD([sQuery(id+"F0.wireOp",EDGE,"E79")])],"isStart":true});
            var Q15;
            Q15=makeQuery(id+"F1.opExtrude","CAP_EDGE",EDGE,{"disambiguationData":[OSD([sQuery(id+"F0.wireOp",EDGE,"E87.MirrorCS")])],"isStart":true});
            var Q16;
            Q16=makeQuery(id+"F1.opExtrude","CAP_EDGE",EDGE,{"disambiguationData":[OSD([sQuery(id+"F0.wireOp",EDGE,"E88.MirrorCS")])],"isStart":true});
            var Q17;
            Q17=makeQuery(id+"F1.opExtrude","CAP_EDGE",EDGE,{"disambiguationData":[OSD([sQuery(id+"F0.wireOp",EDGE,"E86.MirrorCS")])],"isStart":true});
            var Q18;
            Q18=makeQuery(id+"F1.opExtrude","CAP_EDGE",EDGE,{"disambiguationData":[OSD([sQuery(id+"F0.wireOp",EDGE,"E85.MirrorCS")])],"isStart":true});
            var Q19;
            Q19=makeQuery(id+"F1.opExtrude","CAP_EDGE",EDGE,{"disambiguationData":[OSD([sQuery(id+"F0.wireOp",EDGE,"E84.MirrorCS")])],"isStart":true});
            var Q20;
            Q20=makeQuery(id+"F1.opExtrude","CAP_EDGE",EDGE,{"disambiguationData":[OSD([sQuery(id+"F0.wireOp",EDGE,"E128.MirrorCS")])],"isStart":true});
            var Q21;
            Q21=makeQuery(id+"F1.opExtrude","CAP_EDGE",EDGE,{"disambiguationData":[OSD([sQuery(id+"F0.wireOp",EDGE,"E127.MirrorCS")])],"isStart":true});
            var Q22;
            Q22=makeQuery(id+"F1.opExtrude","CAP_EDGE",EDGE,{"disambiguationData":[OSD([sQuery(id+"F0.wireOp",EDGE,"E119")])],"isStart":true});
            var Q23;
            Q23=makeQuery(id+"F1.opExtrude","CAP_EDGE",EDGE,{"disambiguationData":[OSD([sQuery(id+"F0.wireOp",EDGE,"E120")])],"isStart":true});
            var Q24;
            Q24=makeQuery(id+"F1.opExtrude","CAP_EDGE",EDGE,{"disambiguationData":[OSD([sQuery(id+"F0.wireOp",EDGE,"E121")])],"isStart":true});
            var Q25;
            Q25=makeQuery(id+"F1.opExtrude","CAP_EDGE",EDGE,{"disambiguationData":[OSD([sQuery(id+"F0.wireOp",EDGE,"E122")])],"isStart":true});
            var Q26;
            Q26=makeQuery(id+"F1.opExtrude","CAP_EDGE",EDGE,{"disambiguationData":[OSD([sQuery(id+"F0.wireOp",EDGE,"E123")])],"isStart":true});
            var Q27;
            Q27=makeQuery(id+"F1.opExtrude","CAP_EDGE",EDGE,{"disambiguationData":[OSD([sQuery(id+"F0.wireOp",EDGE,"E124.MirrorCS")])],"isStart":true});
            var Q28;
            Q28=makeQuery(id+"F1.opExtrude","CAP_EDGE",EDGE,{"disambiguationData":[OSD([sQuery(id+"F0.wireOp",EDGE,"E125.MirrorCS")])],"isStart":true});
            var Q29;
            Q29=makeQuery(id+"F1.opExtrude","CAP_EDGE",EDGE,{"disambiguationData":[OSD([sQuery(id+"F0.wireOp",EDGE,"E126.MirrorCS")])],"isStart":true});
            var Q30;
            Q30=makeQuery(id+"F1.opExtrude","CAP_EDGE",EDGE,{"disambiguationData":[OSD([sQuery(id+"F0.wireOp",EDGE,"E73")])],"isStart":true});
            var Q31;
            Q31=makeQuery(id+"F1.opExtrude","CAP_EDGE",EDGE,{"disambiguationData":[OSD([sQuery(id+"F0.wireOp",EDGE,"E72")])],"isStart":true});
            var Q32;
            Q32=makeQuery(id+"F1.opExtrude","CAP_EDGE",EDGE,{"disambiguationData":[OSD([sQuery(id+"F0.wireOp",EDGE,"E71")])],"isStart":true});
            var Q33;
            Q33=makeQuery(id+"F1.opExtrude","CAP_EDGE",EDGE,{"disambiguationData":[OSD([sQuery(id+"F0.wireOp",EDGE,"E70")])],"isStart":true});
            var Q34;
            Q34=makeQuery(id+"F1.opExtrude","CAP_EDGE",EDGE,{"disambiguationData":[OSD([sQuery(id+"F0.wireOp",EDGE,"E69")])],"isStart":true});
            var Q35;
            Q35=makeQuery(id+"F1.opExtrude","CAP_EDGE",EDGE,{"disambiguationData":[OSD([sQuery(id+"F0.wireOp",EDGE,"E77.MirrorCS")])],"isStart":true});
            var Q36;
            Q36=makeQuery(id+"F1.opExtrude","CAP_EDGE",EDGE,{"disambiguationData":[OSD([sQuery(id+"F0.wireOp",EDGE,"E78.MirrorCS")])],"isStart":true});
            var Q37;
            Q37=makeQuery(id+"F1.opExtrude","CAP_EDGE",EDGE,{"disambiguationData":[OSD([sQuery(id+"F0.wireOp",EDGE,"E76.MirrorCS")])],"isStart":true});
            var Q38;
            Q38=makeQuery(id+"F1.opExtrude","CAP_EDGE",EDGE,{"disambiguationData":[OSD([sQuery(id+"F0.wireOp",EDGE,"E75.MirrorCS")])],"isStart":true});
            var Q39;
            Q39=makeQuery(id+"F1.opExtrude","CAP_EDGE",EDGE,{"disambiguationData":[OSD([sQuery(id+"F0.wireOp",EDGE,"E74.MirrorCS")])],"isStart":true});
            var Q40;
            Q40=makeQuery(id+"F1.opExtrude","CAP_EDGE",EDGE,{"disambiguationData":[OSD([sQuery(id+"F0.wireOp",EDGE,"E108.MirrorCS")])],"isStart":true});
            var Q41;
            Q41=makeQuery(id+"F1.opExtrude","CAP_EDGE",EDGE,{"disambiguationData":[OSD([sQuery(id+"F0.wireOp",EDGE,"E107.MirrorCS")])],"isStart":true});
            var Q42;
            Q42=makeQuery(id+"F1.opExtrude","CAP_EDGE",EDGE,{"disambiguationData":[OSD([sQuery(id+"F0.wireOp",EDGE,"E99")])],"isStart":true});
            var Q43;
            Q43=makeQuery(id+"F1.opExtrude","CAP_EDGE",EDGE,{"disambiguationData":[OSD([sQuery(id+"F0.wireOp",EDGE,"E100")])],"isStart":true});
            var Q44;
            Q44=makeQuery(id+"F1.opExtrude","CAP_EDGE",EDGE,{"disambiguationData":[OSD([sQuery(id+"F0.wireOp",EDGE,"E101")])],"isStart":true});
            var Q45;
            Q45=makeQuery(id+"F1.opExtrude","CAP_EDGE",EDGE,{"disambiguationData":[OSD([sQuery(id+"F0.wireOp",EDGE,"E102")])],"isStart":true});
            var Q46;
            Q46=makeQuery(id+"F1.opExtrude","CAP_EDGE",EDGE,{"disambiguationData":[OSD([sQuery(id+"F0.wireOp",EDGE,"E103")])],"isStart":true});
            var Q47;
            Q47=makeQuery(id+"F1.opExtrude","CAP_EDGE",EDGE,{"disambiguationData":[OSD([sQuery(id+"F0.wireOp",EDGE,"E104.MirrorCS")])],"isStart":true});
            var Q48;
            Q48=makeQuery(id+"F1.opExtrude","CAP_EDGE",EDGE,{"disambiguationData":[OSD([sQuery(id+"F0.wireOp",EDGE,"E105.MirrorCS")])],"isStart":true});
            var Q49;
            Q49=makeQuery(id+"F1.opExtrude","CAP_EDGE",EDGE,{"disambiguationData":[OSD([sQuery(id+"F0.wireOp",EDGE,"E106.MirrorCS")])],"isStart":true});
            var Q50;
            Q50=makeQuery(id+"F1.opExtrude","CAP_EDGE",EDGE,{"disambiguationData":[OSD([sQuery(id+"F0.wireOp",EDGE,"E114.MirrorCS")])],"isStart":true});
            var Q51;
            Q51=makeQuery(id+"F1.opExtrude","CAP_EDGE",EDGE,{"disambiguationData":[OSD([sQuery(id+"F0.wireOp",EDGE,"E113")])],"isStart":true});
            var Q52;
            Q52=makeQuery(id+"F1.opExtrude","CAP_EDGE",EDGE,{"disambiguationData":[OSD([sQuery(id+"F0.wireOp",EDGE,"E112")])],"isStart":true});
            var Q53;
            Q53=makeQuery(id+"F1.opExtrude","CAP_EDGE",EDGE,{"disambiguationData":[OSD([sQuery(id+"F0.wireOp",EDGE,"E111")])],"isStart":true});
            var Q54;
            Q54=makeQuery(id+"F1.opExtrude","CAP_EDGE",EDGE,{"disambiguationData":[OSD([sQuery(id+"F0.wireOp",EDGE,"E110")])],"isStart":true});
            var Q55;
            Q55=makeQuery(id+"F1.opExtrude","CAP_EDGE",EDGE,{"disambiguationData":[OSD([sQuery(id+"F0.wireOp",EDGE,"E109")])],"isStart":true});
            var Q56;
            Q56=makeQuery(id+"F1.opExtrude","CAP_EDGE",EDGE,{"disambiguationData":[OSD([sQuery(id+"F0.wireOp",EDGE,"E117.MirrorCS")])],"isStart":true});
            var Q57;
            Q57=makeQuery(id+"F1.opExtrude","CAP_EDGE",EDGE,{"disambiguationData":[OSD([sQuery(id+"F0.wireOp",EDGE,"E118.MirrorCS")])],"isStart":true});
            var Q58;
            Q58=makeQuery(id+"F1.opExtrude","CAP_EDGE",EDGE,{"disambiguationData":[OSD([sQuery(id+"F0.wireOp",EDGE,"E116.MirrorCS")])],"isStart":true});
            var Q59;
            Q59=makeQuery(id+"F1.opExtrude","CAP_EDGE",EDGE,{"disambiguationData":[OSD([sQuery(id+"F0.wireOp",EDGE,"E115.MirrorCS")])],"isStart":true});
            fillet(context, id + "F3", {"entities" : qUnion([Q0, Q1, Q2, Q3, Q4, Q5, Q6, Q7, Q8, Q9, Q10, Q11, Q12, Q13, Q14, Q15, Q16, Q17, Q18, Q19, Q20, Q21, Q22, Q23, Q24, Q25, Q26, Q27, Q28, Q29, Q30, Q31, Q32, Q33, Q34, Q35, Q36, Q37, Q38, Q39, Q40, Q41, Q42, Q43, Q44, Q45, Q46, Q47, Q48, Q49, Q50, Q51, Q52, Q53, Q54, Q55, Q56, Q57, Q58, Q59]), "radius" : 2 * mm, "tangentPropagation" : true, "allowEdgeOverflow" : false});
        }
        {
            var Q0;
            Q0=makeQuery(id+"F1.opExtrude","CAP_EDGE",EDGE,{"disambiguationData":[OSD([sQuery(id+"F0.wireOp",EDGE,"E5")])],"isStart":true});
            var Q1;
            Q1=makeQuery(id+"F1.opExtrude","CAP_EDGE",EDGE,{"disambiguationData":[OSD([sQuery(id+"F0.wireOp",EDGE,"E4")])],"isStart":true});
            var Q2;
            Q2=makeQuery(id+"F1.opExtrude","CAP_EDGE",EDGE,{"disambiguationData":[OSD([sQuery(id+"F0.wireOp",EDGE,"E3")])],"isStart":true});
            var Q3;
            Q3=makeQuery(id+"F1.opExtrude","CAP_EDGE",EDGE,{"disambiguationData":[OSD([sQuery(id+"F0.wireOp",EDGE,"E6")])],"isStart":true});
            var Q4;
            Q4=makeQuery(id+"F1.opExtrude","CAP_EDGE",EDGE,{"disambiguationData":[OSD([sQuery(id+"F0.wireOp",EDGE,"E8.MirrorCS")])],"isStart":true});
            var Q5;
            Q5=makeQuery(id+"F1.opExtrude","CAP_EDGE",EDGE,{"disambiguationData":[OSD([sQuery(id+"F0.wireOp",EDGE,"E9.MirrorCS")])],"isStart":true});
            var Q6;
            Q6=makeQuery(id+"F1.opExtrude","CAP_EDGE",EDGE,{"disambiguationData":[OSD([sQuery(id+"F0.wireOp",EDGE,"E10.MirrorCS")])],"isStart":true});
            var Q7;
            Q7=makeQuery(id+"F1.opExtrude","CAP_EDGE",EDGE,{"disambiguationData":[OSD([sQuery(id+"F0.wireOp",EDGE,"E11.MirrorCS")])],"isStart":true});
            var Q8;
            Q8=makeQuery(id+"F1.opExtrude","CAP_EDGE",EDGE,{"disambiguationData":[OSD([sQuery(id+"F0.wireOp",EDGE,"E2")])],"isStart":true});
            var Q9;
            {var subQ0=sQuery(id+"F0.wireOp",EDGE,"E23");Q9=makeQuery(id+"F1.opExtrude","CAP_EDGE",EDGE,{"disambiguationData":[OSD([subQ0]),TDD([makeQuery(id+"F0.imprint","IMPRINT",EDGE,{"disambiguationData":[TD([[makeQuery(id+"F0.imprint","INTERSECT",VERTEX,{"derivedFrom":[subQ0,sQuery(id+"F0.wireOp",EDGE,"E26.MirrorCS")]}),1.0]])],"derivedFrom":subQ0})])],"isStart":true});}
            var Q10;
            {var subQ0=sQuery(id+"F0.wireOp",EDGE,"E23");Q10=makeQuery(id+"F1.opExtrude","CAP_EDGE",EDGE,{"disambiguationData":[OSD([subQ0]),TDD([makeQuery(id+"F0.imprint","IMPRINT",EDGE,{"disambiguationData":[TD([[makeQuery(id+"F0.imprint","INTERSECT",VERTEX,{"derivedFrom":[subQ0,sQuery(id+"F0.wireOp",EDGE,"E24")]}),-1.0]])],"derivedFrom":subQ0})])],"isStart":true});}
            var Q11;
            Q11=makeQuery(id+"F1.opExtrude","CAP_EDGE",EDGE,{"disambiguationData":[OSD([sQuery(id+"F0.wireOp",EDGE,"E22")])],"isStart":true});
            var Q12;
            Q12=makeQuery(id+"F1.opExtrude","CAP_EDGE",EDGE,{"disambiguationData":[OSD([sQuery(id+"F0.wireOp",EDGE,"E12.MirrorCS")])],"isStart":true});
            var Q13;
            Q13=makeQuery(id+"F1.opExtrude","CAP_EDGE",EDGE,{"disambiguationData":[OSD([sQuery(id+"F0.wireOp",EDGE,"E20.MirrorCS")])],"isStart":true});
            var Q14;
            Q14=makeQuery(id+"F1.opExtrude","CAP_EDGE",EDGE,{"disambiguationData":[OSD([sQuery(id+"F0.wireOp",EDGE,"E19.MirrorCS")])],"isStart":true});
            var Q15;
            Q15=makeQuery(id+"F1.opExtrude","CAP_EDGE",EDGE,{"disambiguationData":[OSD([sQuery(id+"F0.wireOp",EDGE,"E18.MirrorCS")])],"isStart":true});
            var Q16;
            Q16=makeQuery(id+"F1.opExtrude","CAP_EDGE",EDGE,{"disambiguationData":[OSD([sQuery(id+"F0.wireOp",EDGE,"E13.MirrorCS")])],"isStart":true});
            var Q17;
            Q17=makeQuery(id+"F1.opExtrude","CAP_EDGE",EDGE,{"disambiguationData":[OSD([sQuery(id+"F0.wireOp",EDGE,"E16.MirrorCS")])],"isStart":true});
            var Q18;
            Q18=makeQuery(id+"F1.opExtrude","CAP_EDGE",EDGE,{"disambiguationData":[OSD([sQuery(id+"F0.wireOp",EDGE,"E14.MirrorCS")])],"isStart":true});
            var Q19;
            Q19=makeQuery(id+"F1.opExtrude","CAP_EDGE",EDGE,{"disambiguationData":[OSD([sQuery(id+"F0.wireOp",EDGE,"E17.MirrorCS")])],"isStart":true});
            fillet(context, id + "F4", {"entities" : qUnion([Q0, Q1, Q2, Q3, Q4, Q5, Q6, Q7, Q8, Q9, Q10, Q11, Q12, Q13, Q14, Q15, Q16, Q17, Q18, Q19]), "radius" : .7 * mm, "tangentPropagation" : true, "allowEdgeOverflow" : false});
        }
    });
